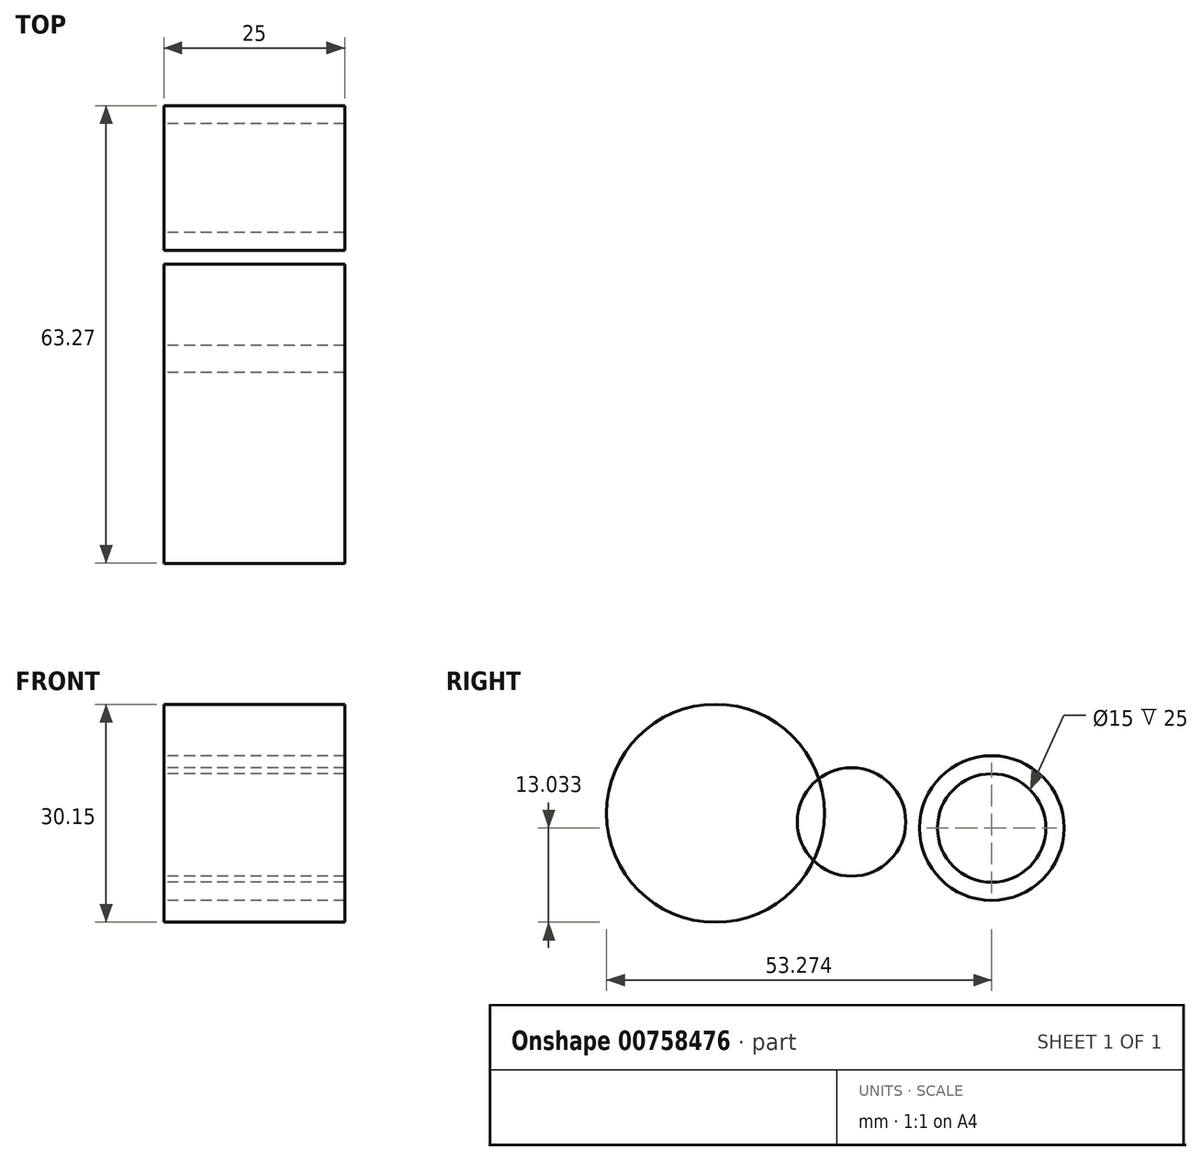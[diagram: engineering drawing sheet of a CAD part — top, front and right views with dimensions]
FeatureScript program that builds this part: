
annotation { "Feature Type Name" : "Feature", "Feature Type Description" : "" }
export const myFeature = defineFeature(function(context is Context, id is Id, definition is map)
    precondition{}
    {
        {
            var Q0;
            Q0=qCreatedBy(makeId("Right.planeOp"),FACE);
            var sketch = newSketch(context, id + "F0", { "sketchPlane" : qUnion([Q0])});
            skCircle(sketch, "E0", {"center": v(-53.81, 31.58) * mm, "radius": 15.07 * mm});
            skSolve(sketch);
        }
        {
            var Q0;
            Q0=qCreatedBy(makeId("Right.planeOp"),FACE);
            var sketch = newSketch(context, id + "F1", { "sketchPlane" : qUnion([Q0])});
            skCircle(sketch, "E1", {"center": v(-35, 30.39) * mm, "radius": 7.5 * mm});
            skSolve(sketch);
        }
        {
            var Q0;
            Q0=qCreatedBy(makeId("Right.planeOp"),FACE);
            var sketch = newSketch(context, id + "F2", { "sketchPlane" : qUnion([Q0])});
            skCircle(sketch, "E2", {"center": v(-15.6, 29.54) * mm, "radius": 10 * mm});
            skCircle(sketch, "E3", {"center": v(-15.6, 29.54) * mm, "radius": 7.5 * mm});
            skSolve(sketch);
        }
        {
            var Q0;
            Q0=makeQuery(id+"F0.imprint","IMPRINT",FACE,{"disambiguationData":[TD([[makeQuery(id+"F0.imprint","IMPRINT",EDGE,{"derivedFrom":sQuery(id+"F0.wireOp",EDGE,"E0")}),1.0]])]});
            extrude(context, id + "F3", {"entities" : qUnion([Q0]), "depth" : 25 * mm, "offsetDistance" : 25 * mm});
        }
        {
            var Q0;
            Q0=makeQuery(id+"F1.imprint","IMPRINT",FACE,{"disambiguationData":[TD([[makeQuery(id+"F1.imprint","IMPRINT",EDGE,{"derivedFrom":sQuery(id+"F1.wireOp",EDGE,"E1")}),1.0]])]});
            extrude(context, id + "F4", {"entities" : qUnion([Q0]), "depth" : 25 * mm, "offsetDistance" : 25 * mm});
        }
        {
            var Q0;
            Q0=makeQuery(id+"F2.imprint","IMPRINT",FACE,{"disambiguationData":[TD([[makeQuery(id+"F2.imprint","IMPRINT",EDGE,{"derivedFrom":sQuery(id+"F2.wireOp",EDGE,"E2")}),1.0]])]});
            extrude(context, id + "F5", {"entities" : qUnion([Q0]), "depth" : 25 * mm, "offsetDistance" : 25 * mm});
        }
    });
